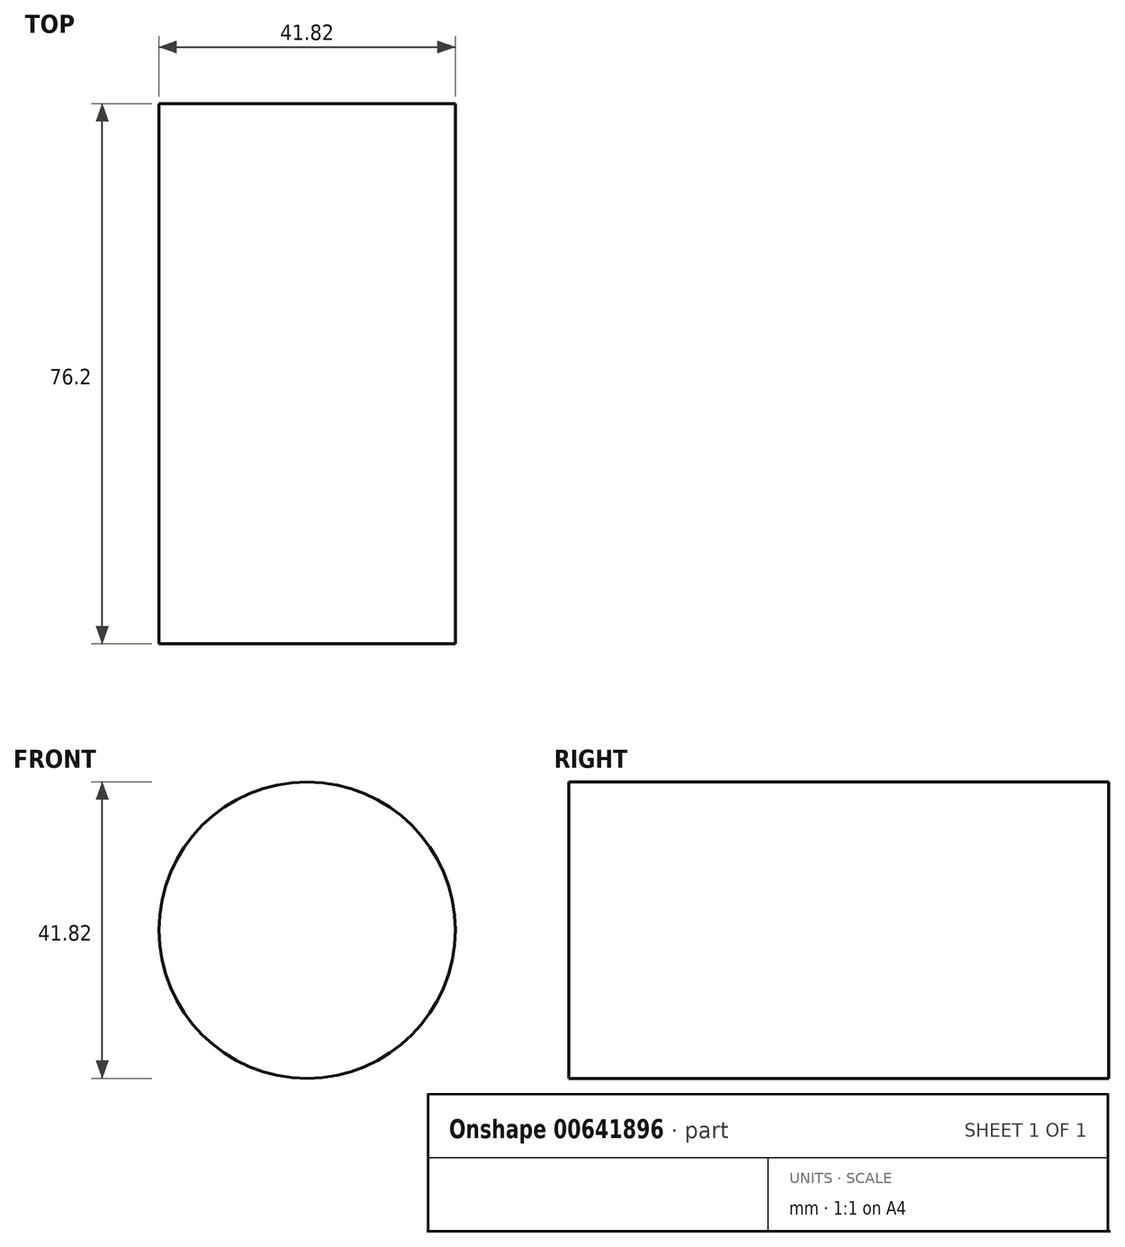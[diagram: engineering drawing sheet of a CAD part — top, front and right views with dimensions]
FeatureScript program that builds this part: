
annotation { "Feature Type Name" : "Feature", "Feature Type Description" : "" }
export const myFeature = defineFeature(function(context is Context, id is Id, definition is map)
    precondition{}
    {
        {
            var Q0;
            Q0=qCreatedBy(makeId("Front.planeOp"),FACE);
            var sketch = newSketch(context, id + "F0", { "sketchPlane" : qUnion([Q0])});
            skCircle(sketch, "E0", {"center": v(0, 0) * mm, "radius": 20.91 * mm});
            skSolve(sketch);
        }
        {
            var Q0;
            Q0=makeQuery(id+"F0.imprint","IMPRINT",FACE,{"disambiguationData":[TD([[makeQuery(id+"F0.imprint","IMPRINT",EDGE,{"derivedFrom":sQuery(id+"F0.wireOp",EDGE,"E0")}),1.0]])]});
            extrude(context, id + "F1", {"entities" : qUnion([Q0]), "depth" : 76.2 * mm, "offsetDistance" : 25.4 * mm});
        }
    });
